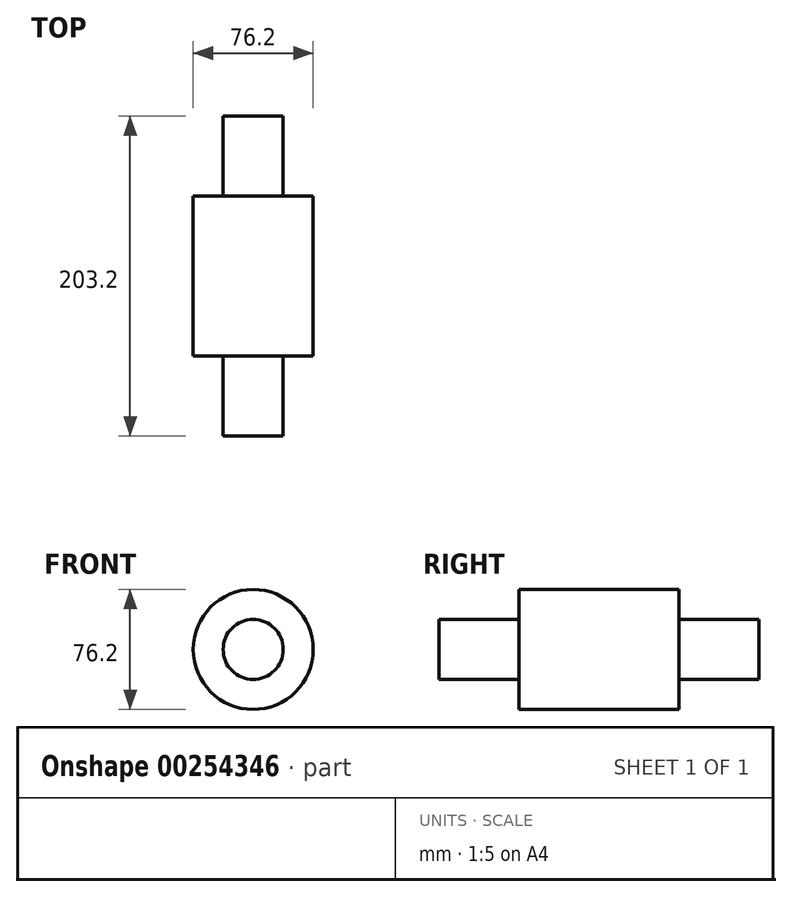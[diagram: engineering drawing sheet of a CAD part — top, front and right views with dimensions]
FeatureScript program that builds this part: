
annotation { "Feature Type Name" : "Feature", "Feature Type Description" : "" }
export const myFeature = defineFeature(function(context is Context, id is Id, definition is map)
    precondition{}
    {
        {
            var Q0;
            Q0=qCreatedBy(makeId("Front.planeOp"),FACE);
            var sketch = newSketch(context, id + "F0", { "sketchPlane" : qUnion([Q0])});
            skCircle(sketch, "E0", {"center": v(0, 0) * mm, "radius": 38.1 * mm});
            skSolve(sketch);
        }
        {
            var Q0;
            Q0=makeQuery(id+"F0.imprint","IMPRINT",FACE,{"disambiguationData":[TD([[makeQuery(id+"F0.imprint","IMPRINT",EDGE,{"derivedFrom":sQuery(id+"F0.wireOp",EDGE,"E0")}),1.0]])]});
            var sketch = newSketch(context, id + "F1", { "sketchPlane" : qUnion([Q0])});
            skCircle(sketch, "E1", {"center": v(0, 0) * mm, "radius": 19.05 * mm});
            skSolve(sketch);
        }
        {
            var Q0;
            Q0 = qSketchRegion(id + "F0", true);
            extrude(context, id + "F2", {"entities" : qUnion([Q0]), "endBound" : BoundingType.SYMMETRIC, "depth" : 101.6 * mm});
        }
        {
            var Q0;
            Q0 = qSketchRegion(id + "F1", true);
            extrude(context, id + "F3", {"entities" : qUnion([Q0]), "operationType" : NewBodyOperationType.ADD, "endBound" : BoundingType.SYMMETRIC, "depth" : 203.2 * mm});
        }
    });
